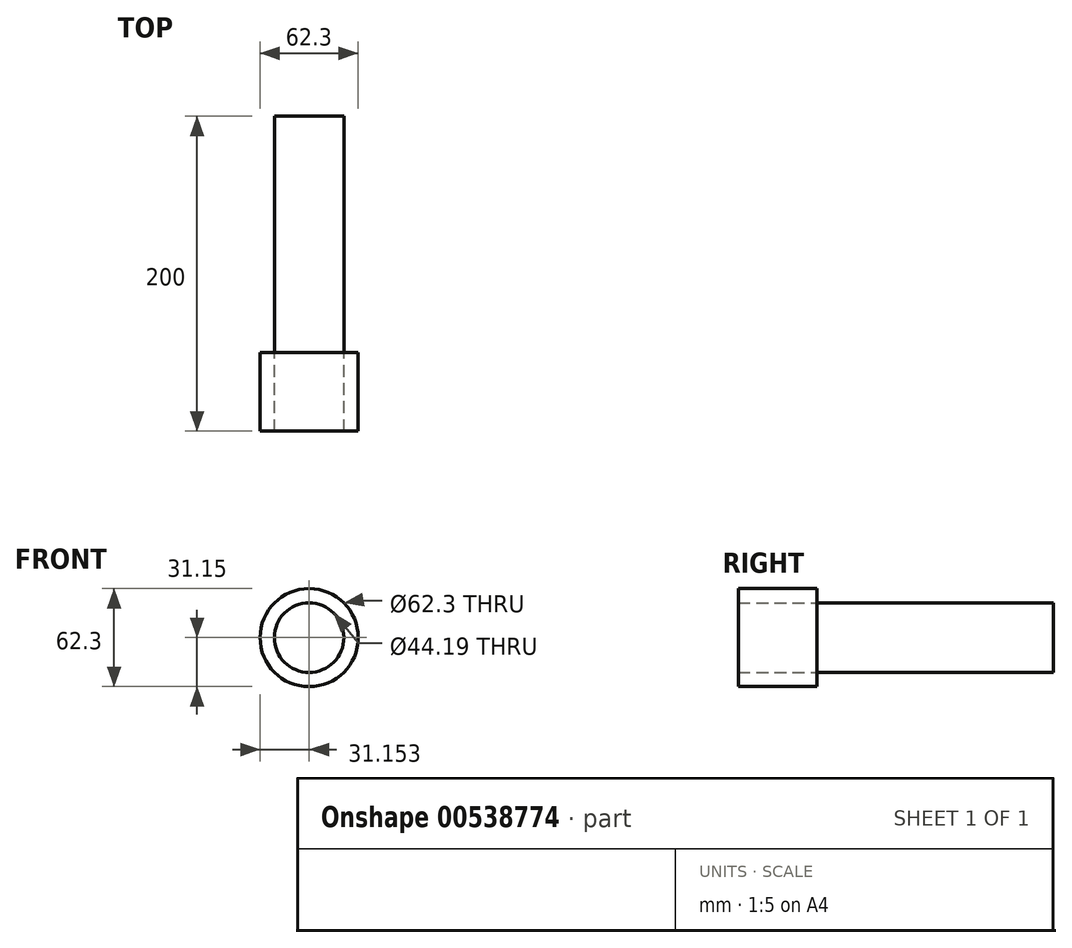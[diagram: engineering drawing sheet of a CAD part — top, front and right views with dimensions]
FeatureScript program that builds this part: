
annotation { "Feature Type Name" : "Feature", "Feature Type Description" : "" }
export const myFeature = defineFeature(function(context is Context, id is Id, definition is map)
    precondition{}
    {
        {
            var Q0;
            Q0=qCreatedBy(makeId("Front.planeOp"),FACE);
            var sketch = newSketch(context, id + "F0", { "sketchPlane" : qUnion([Q0])});
            skCircle(sketch, "E0", {"center": v(-40.12, 25.75) * mm, "radius": 31.15 * mm});
            skCircle(sketch, "E1", {"center": v(-40.12, 25.75) * mm, "radius": 22.1 * mm});
            skSolve(sketch);
        }
        {
            var Q0;
            Q0=sQuery(id+"F0.wireOp",EDGE,"E1");
            extrude(context, id + "F1", {"bodyType" : ToolBodyType.SURFACE, "surfaceEntities" : qUnion([Q0]), "depth" : -200 * mm, "offsetDistance" : 25 * mm});
        }
        {
            var Q0;
            Q0=sQuery(id+"F0.wireOp",EDGE,"E0");
            extrude(context, id + "F2", {"bodyType" : ToolBodyType.SURFACE, "surfaceEntities" : qUnion([Q0]), "depth" : -50 * mm, "offsetDistance" : 25 * mm});
        }
    });
